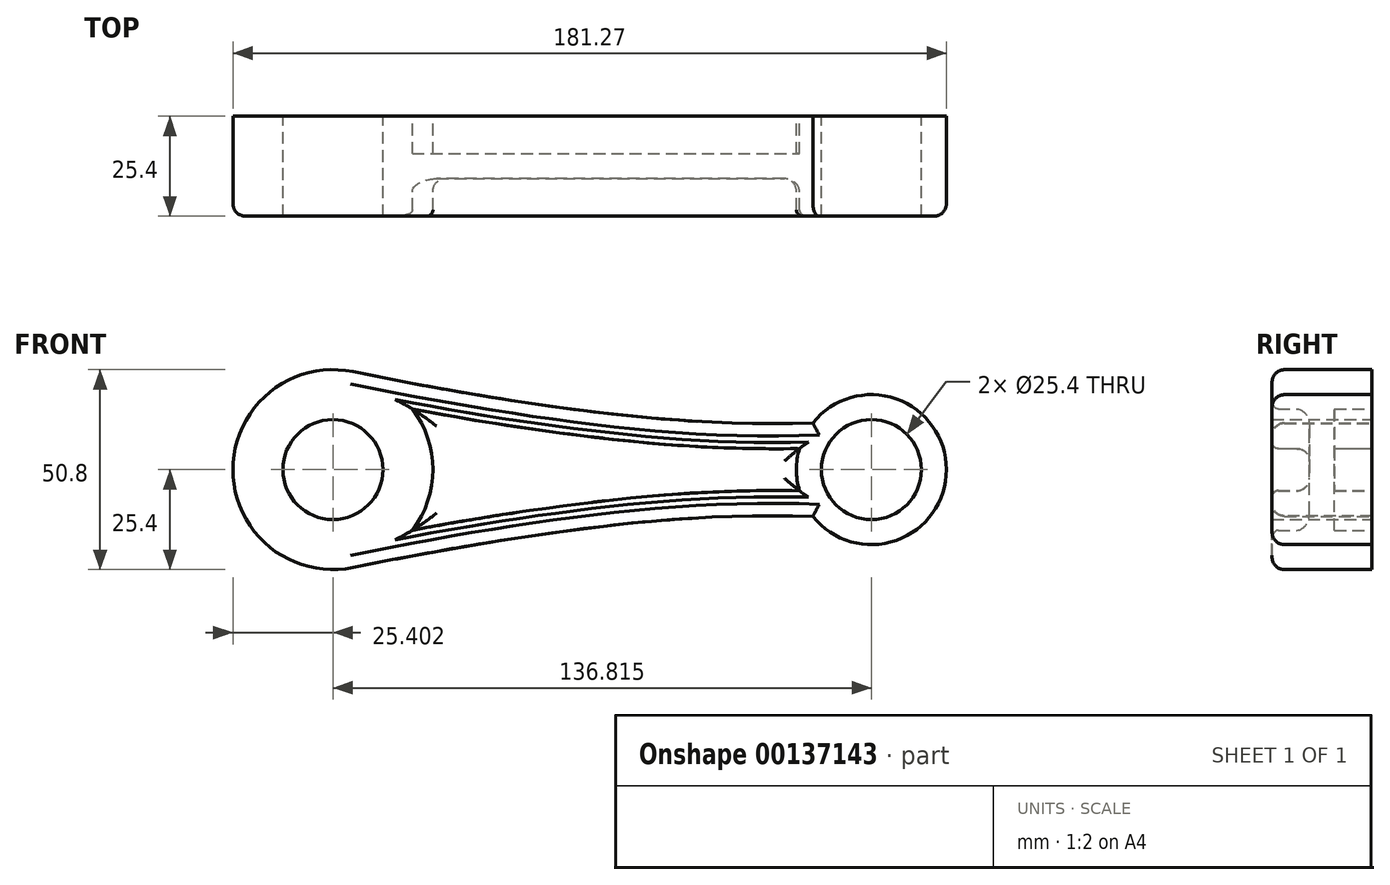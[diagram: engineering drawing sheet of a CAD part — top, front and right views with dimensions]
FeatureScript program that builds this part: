
annotation { "Feature Type Name" : "Feature", "Feature Type Description" : "" }
export const myFeature = defineFeature(function(context is Context, id is Id, definition is map)
    precondition{}
    {
        {
            var Q0;
            Q0=qCreatedBy(makeId("Front.planeOp"),FACE);
            var sketch = newSketch(context, id + "F0", { "sketchPlane" : qUnion([Q0])});
            skCircle(sketch, "E0", {"center": v(-86.53, 0) * mm, "radius": 25.4 * mm});
            skCircle(sketch, "E1", {"center": v(50.29, 0) * mm, "radius": 12.7 * mm});
            skFitSpline(sketch, "E2", {"points": [v(-81.43, 24.88) * mm, v(0, 12.66) * mm, v(48.47, 12.57) * mm], "startDerivative": vector(151.5, -31.07) * mm, "endDerivative": vector(104.27, 6.97) * mm});
            skLineSegment(sketch, "E3", {"start": v(-86.53, 0) * mm, "end": v(50.29, 0) * mm, "construction": true});
            skFitSpline(sketch, "E4.MirrorCS", {"points": [v(-81.43, -24.88) * mm, v(0, -12.66) * mm, v(48.47, -12.57) * mm], "startDerivative": vector(151.5, 31.07) * mm, "endDerivative": vector(104.27, -6.97) * mm});
            skFitSpline(sketch, "E5.0", {"points": [v(-82.7, 18.66) * mm, v(-76.35, 17.36) * mm, v(-63.59, 14.88) * mm, v(-44.66, 11.63) * mm, v(-29.37, 9.4) * mm, v(-17.61, 7.96) * mm, v(-9.07, 7.05) * mm, v(-0.85, 6.33) * mm, v(7, 5.82) * mm, v(14.52, 5.5) * mm, v(24.16, 5.31) * mm, v(35.64, 5.47) * mm, v(44.49, 5.94) * mm, v(48.9, 6.23) * mm]});
            skFitSpline(sketch, "E6.0", {"points": [v(-82.7, -18.66) * mm, v(-76.35, -17.36) * mm, v(-63.59, -14.88) * mm, v(-44.66, -11.63) * mm, v(-29.37, -9.4) * mm, v(-17.61, -7.96) * mm, v(-9.07, -7.05) * mm, v(-0.85, -6.33) * mm, v(7, -5.82) * mm, v(14.52, -5.5) * mm, v(24.16, -5.31) * mm, v(35.64, -5.47) * mm, v(44.49, -5.94) * mm, v(48.9, -6.23) * mm]});
            skCircle(sketch, "E7.0", {"center": v(50.29, 0) * mm, "radius": 19.05 * mm});
            skCircle(sketch, "E8", {"center": v(-86.53, 0) * mm, "radius": 12.7 * mm});
            skSolve(sketch);
        }
        {
            var Q0;
            {var subQ0=sQuery(id+"F0.wireOp",EDGE,"E5.0");Q0=makeQuery(id+"F0.imprint","IMPRINT",FACE,{"disambiguationData":[TD([[makeQuery(id+"F0.imprint","IMPRINT",EDGE,{"derivedFrom":subQ0}),-1.0]])]});}
            extrude(context, id + "F1", {"entities" : qUnion([Q0]), "endBound" : BoundingType.SYMMETRIC, "depth" : 6.35 * mm});
        }
        {
            var Q0;
            {var subQ0=sQuery(id+"F0.wireOp",EDGE,"E2");Q0=makeQuery(id+"F0.imprint","IMPRINT",FACE,{"disambiguationData":[TD([[makeQuery(id+"F0.imprint","IMPRINT",EDGE,{"derivedFrom":subQ0}),-1.0]])]});}
            var Q1;
            {var subQ0=sQuery(id+"F0.wireOp",EDGE,"E4.MirrorCS");Q1=makeQuery(id+"F0.imprint","IMPRINT",FACE,{"disambiguationData":[TD([[makeQuery(id+"F0.imprint","IMPRINT",EDGE,{"derivedFrom":subQ0}),1.0]])]});}
            var Q2;
            Q2=makeQuery(id+"F0.imprint","IMPRINT",FACE,{"disambiguationData":[TD([[makeQuery(id+"F0.imprint","IMPRINT",EDGE,{"derivedFrom":sQuery(id+"F0.wireOp",EDGE,"E1")}),-1.0]])]});
            var Q3;
            Q3=makeQuery(id+"F0.imprint","IMPRINT",FACE,{"disambiguationData":[TD([[makeQuery(id+"F0.imprint","IMPRINT",EDGE,{"derivedFrom":sQuery(id+"F0.wireOp",EDGE,"E8")}),-1.0]])]});
            extrude(context, id + "F2", {"entities" : qUnion([Q0, Q1, Q2, Q3]), "operationType" : NewBodyOperationType.ADD, "endBound" : BoundingType.SYMMETRIC, "depth" : 25.4 * mm});
        }
        {
            var Q0;
            Q0=makeQuery(id+"F2.opExtrude","CAP_EDGE",EDGE,{"disambiguationData":[OSD([sQuery(id+"F0.wireOp",EDGE,"E2")])],"isStart":false});
            var Q1;
            {var subQ0=sQuery(id+"F0.wireOp",EDGE,"E7.0");Q1=makeQuery(id+"F2.opExtrude","CAP_EDGE",EDGE,{"disambiguationData":[OSD([subQ0]),TDD([makeQuery(id+"F0.imprint","IMPRINT",EDGE,{"disambiguationData":[TD([[makeQuery(id+"F0.imprint","INTERSECT",VERTEX,{"derivedFrom":[sQuery(id+"F0.wireOp",EDGE,"E2"),subQ0]}),1.0]])],"derivedFrom":subQ0})])],"isStart":false});}
            fillet(context, id + "F3", {"entities" : qUnion([Q0, Q1]), "radius" : 3.17 * mm, "tangentPropagation" : true, "allowEdgeOverflow" : false});
        }
        {
            var Q0;
            Q0=makeQuery(id+"F1.opExtrude","CAP_FACE",FACE,{"disambiguationData":[OSD([sQuery(id+"F0.wireOp",EDGE,"E0"),sQuery(id+"F0.wireOp",EDGE,"E5.0"),sQuery(id+"F0.wireOp",EDGE,"E6.0"),sQuery(id+"F0.wireOp",EDGE,"E7.0")])],"isStart":false});
            fillet(context, id + "F4", {"entities" : qUnion([Q0]), "radius" : 3.17 * mm, "tangentPropagation" : true, "allowEdgeOverflow" : false});
        }
        {
            var Q0;
            Q0=makeQuery(id+"F2.opExtrude","CAP_EDGE",EDGE,{"disambiguationData":[OSD([sQuery(id+"F0.wireOp",EDGE,"E5.0")])],"isStart":false});
            var Q1;
            {var subQ0=sQuery(id+"F0.wireOp",EDGE,"E0");Q1=makeQuery(id+"F2.opExtrude","CAP_EDGE",EDGE,{"disambiguationData":[OSD([subQ0]),TDD([makeQuery(id+"F0.imprint","IMPRINT",EDGE,{"disambiguationData":[TD([[makeQuery(id+"F0.imprint","INTERSECT",VERTEX,{"derivedFrom":[subQ0,sQuery(id+"F0.wireOp",EDGE,"E5.0")]}),1.0]])],"derivedFrom":subQ0})])],"isStart":false});}
            var Q2;
            Q2=makeQuery(id+"F2.opExtrude","CAP_EDGE",EDGE,{"disambiguationData":[OSD([sQuery(id+"F0.wireOp",EDGE,"E6.0")])],"isStart":false});
            var Q3;
            {var subQ0=sQuery(id+"F0.wireOp",EDGE,"E7.0");Q3=makeQuery(id+"F2.opExtrude","CAP_EDGE",EDGE,{"disambiguationData":[OSD([subQ0]),TDD([makeQuery(id+"F0.imprint","IMPRINT",EDGE,{"disambiguationData":[TD([[makeQuery(id+"F0.imprint","INTERSECT",VERTEX,{"derivedFrom":[sQuery(id+"F0.wireOp",EDGE,"E5.0"),subQ0]}),-1.0]])],"derivedFrom":subQ0})])],"isStart":false});}
            fillet(context, id + "F5", {"entities" : qUnion([Q0, Q1, Q2, Q3]), "radius" : 1.57 * mm, "tangentPropagation" : true, "allowEdgeOverflow" : false});
        }
    });
